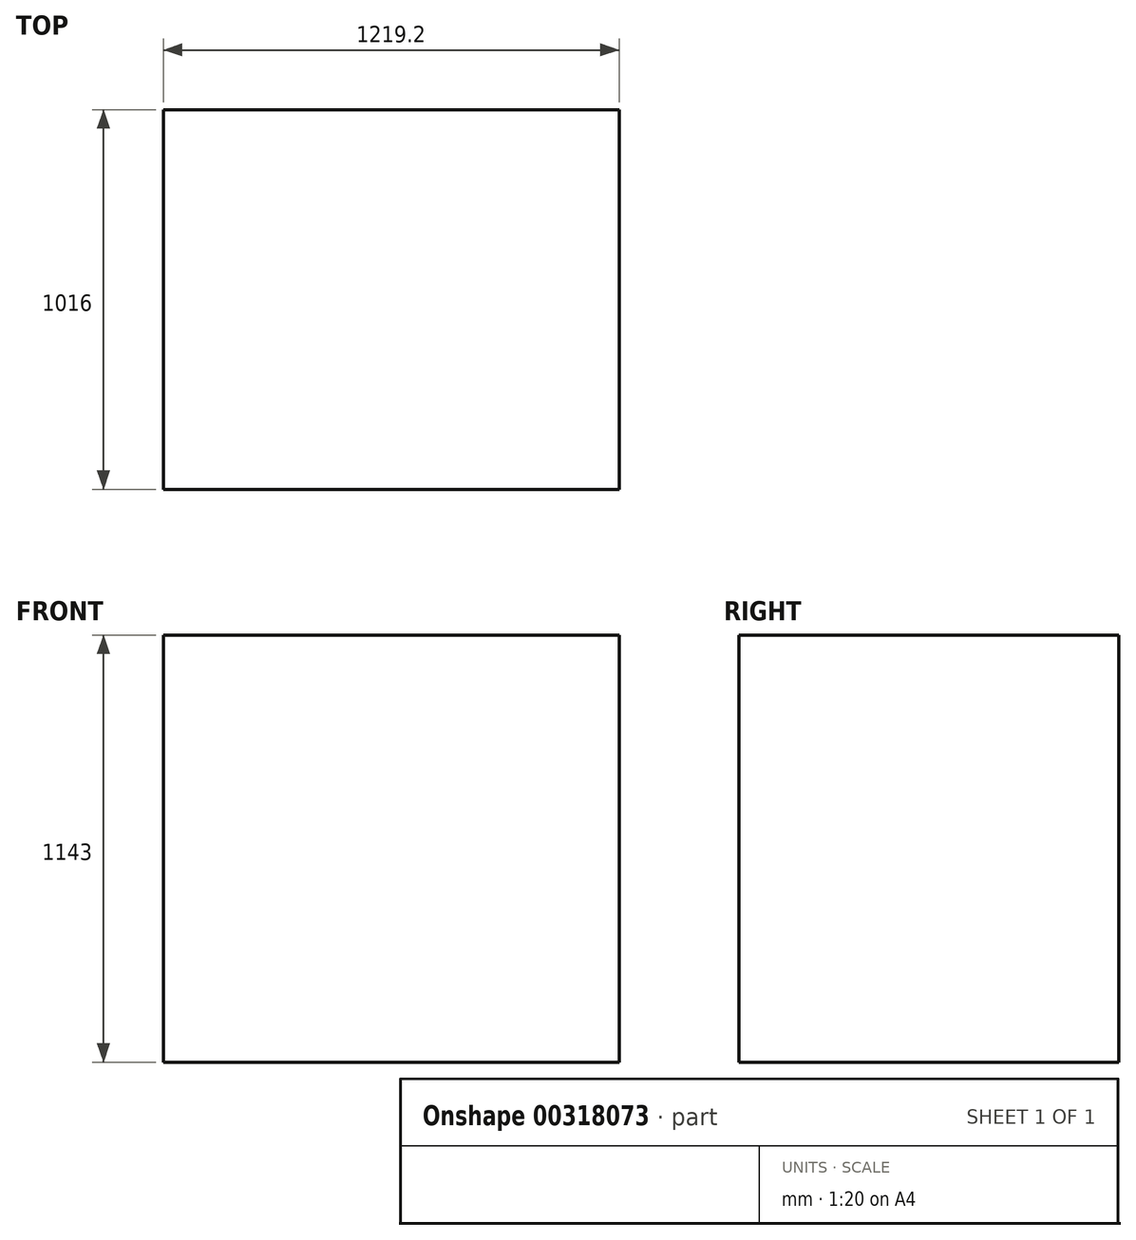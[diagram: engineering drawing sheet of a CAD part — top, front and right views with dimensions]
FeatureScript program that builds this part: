
annotation { "Feature Type Name" : "Feature", "Feature Type Description" : "" }
export const myFeature = defineFeature(function(context is Context, id is Id, definition is map)
    precondition{}
    {
        {
            var Q0;
            Q0=qCreatedBy(makeId("Front.planeOp"),FACE);
            var sketch = newSketch(context, id + "F0", { "sketchPlane" : qUnion([Q0])});
            skLineSegment(sketch, "E0.bottom", {"start": v(-1219.2, 1143) * mm, "end": v(0, 1143) * mm});
            skLineSegment(sketch, "E0.top", {"start": v(-1219.2, 0) * mm, "end": v(0, 0) * mm});
            skLineSegment(sketch, "E0.left", {"start": v(-1219.2, 1143) * mm, "end": v(-1219.2, 0) * mm});
            skLineSegment(sketch, "E0.right", {"start": v(0, 1143) * mm, "end": v(0, 0) * mm});
            skSolve(sketch);
        }
        {
            var Q0;
            Q0=qSketchRegion(id+"F0",true);
            extrude(context, id + "F1", {"entities" : qUnion([Q0]), "depth" : 1016 * mm, "offsetDistance" : 25.4 * mm});
        }
    });
